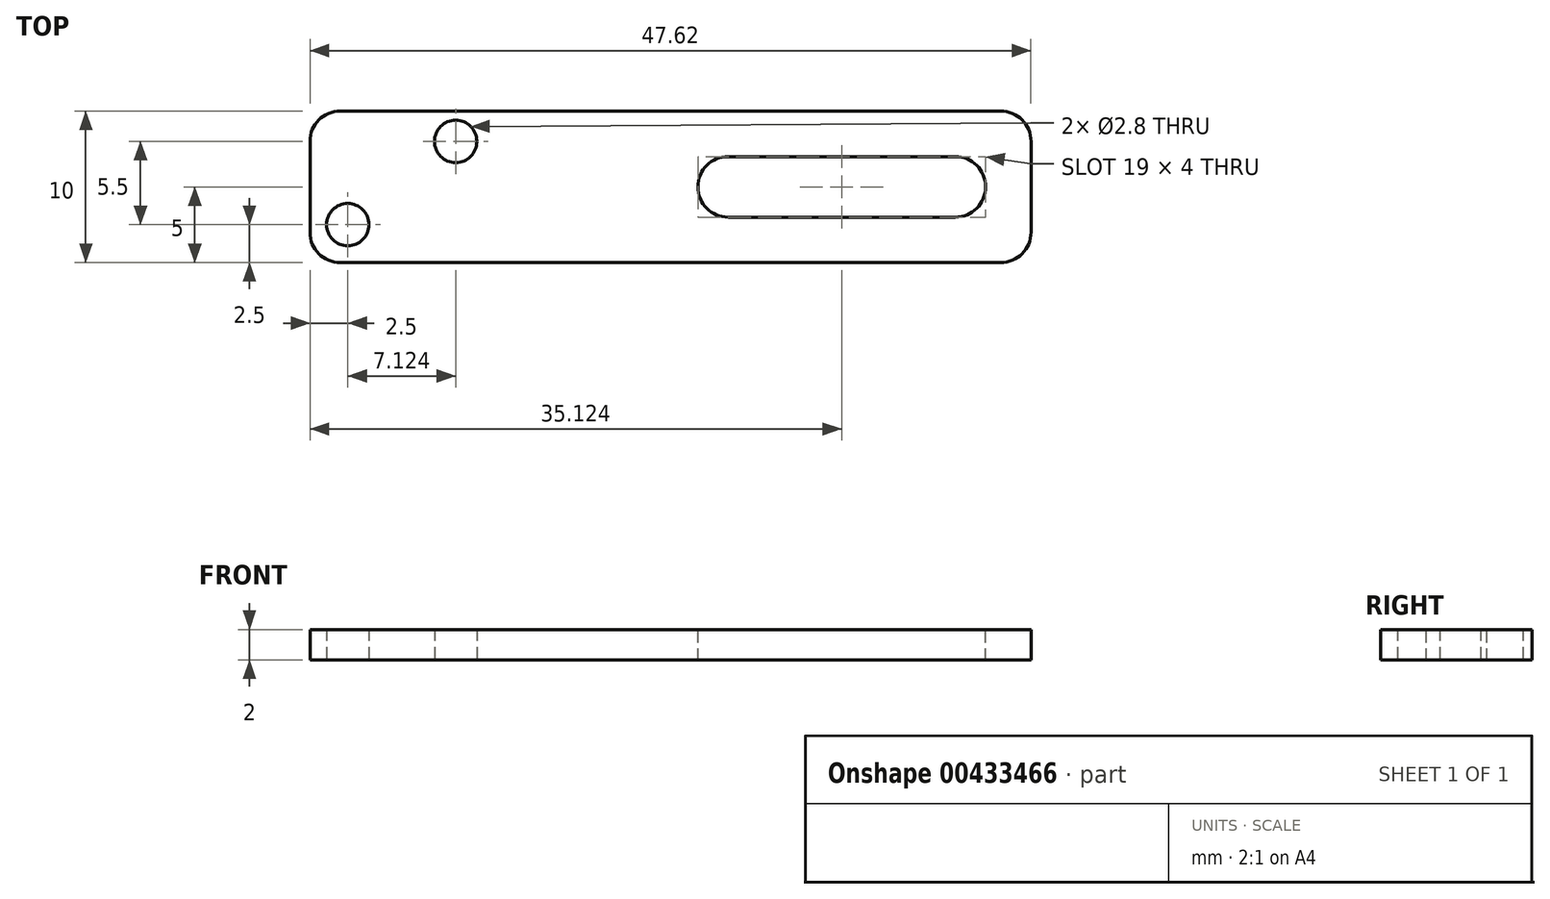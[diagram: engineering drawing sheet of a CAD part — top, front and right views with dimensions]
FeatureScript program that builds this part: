
annotation { "Feature Type Name" : "Feature", "Feature Type Description" : "" }
export const myFeature = defineFeature(function(context is Context, id is Id, definition is map)
    precondition{}
    {
        {
            var Q0;
            Q0=qCreatedBy(makeId("Top.planeOp"),FACE);
            var sketch = newSketch(context, id + "F0", { "sketchPlane" : qUnion([Q0])});
            skLineSegment(sketch, "E0", {"start": v(47.62, 10) * mm, "end": v(13.02, 10) * mm});
            skLineSegment(sketch, "E1", {"start": v(13.02, 10) * mm, "end": v(13.02, 10) * mm});
            skLineSegment(sketch, "E2", {"start": v(13.02, 10) * mm, "end": v(0, 10) * mm});
            skLineSegment(sketch, "E3", {"start": v(0, 10) * mm, "end": v(0, 0) * mm});
            skLineSegment(sketch, "E4", {"start": v(0, 0) * mm, "end": v(47.62, 0) * mm});
            skLineSegment(sketch, "E5", {"start": v(47.62, 0) * mm, "end": v(47.62, 10) * mm});
            skCircle(sketch, "E6", {"center": v(9.62, 8) * mm, "radius": 1.4 * mm});
            skCircle(sketch, "E7", {"center": v(2.5, 2.5) * mm, "radius": 1.4 * mm});
            skSolve(sketch);
        }
        {
            var Q0;
            Q0 = qSketchRegion(id + "F0", true);
            extrude(context, id + "F1", {"entities" : qUnion([Q0]), "depth" : 2 * mm});
        }
        {
            var Q0;
            Q0=makeQuery(id+"F1.opExtrude","SWEPT_EDGE",EDGE,{"disambiguationData":[OSD([sQuery(id+"F0.wireOp",EDGE,"E3"),sQuery(id+"F0.wireOp",EDGE,"E4")])]});
            var Q1;
            Q1=makeQuery(id+"F1.opExtrude","SWEPT_EDGE",EDGE,{"disambiguationData":[OSD([sQuery(id+"F0.wireOp",EDGE,"E2"),sQuery(id+"F0.wireOp",EDGE,"E3")])]});
            var Q2;
            Q2=makeQuery(id+"F1.opExtrude","SWEPT_EDGE",EDGE,{"disambiguationData":[OSD([sQuery(id+"F0.wireOp",EDGE,"E4"),sQuery(id+"F0.wireOp",EDGE,"E5")])]});
            var Q3;
            Q3=makeQuery(id+"F1.opExtrude","SWEPT_EDGE",EDGE,{"disambiguationData":[OSD([sQuery(id+"F0.wireOp",EDGE,"E0"),sQuery(id+"F0.wireOp",EDGE,"E5")])]});
            fillet(context, id + "F2", {"entities" : qUnion([Q0, Q1, Q2, Q3]), "radius" : 2 * mm, "tangentPropagation" : true, "allowEdgeOverflow" : false});
        }
        {
            var Q0;
            Q0=makeQuery(id+"F1.opExtrude","CAP_FACE",FACE,{"disambiguationData":[OSD([sQuery(id+"F0.wireOp",EDGE,"E0"),sQuery(id+"F0.wireOp",EDGE,"E2"),sQuery(id+"F0.wireOp",EDGE,"E3"),sQuery(id+"F0.wireOp",EDGE,"E4"),sQuery(id+"F0.wireOp",EDGE,"E5"),sQuery(id+"F0.wireOp",EDGE,"E6"),sQuery(id+"F0.wireOp",EDGE,"E7")])],"isStart":false});
            var sketch = newSketch(context, id + "F3", { "sketchPlane" : qUnion([Q0])});
            skLineSegment(sketch, "E8", {"start": v(42.62, 5) * mm, "end": v(27.62, 5) * mm, "construction": true});
            skPoint(sketch, "E8.startSnap0", {"position": v(47.62, 5) * mm});
            skArc(sketch, "E9.0.startCap", {"start": v(42.62, 7) * mm, "mid": v(44.62, 5) * mm, "end": v(42.62, 3) * mm});
            skArc(sketch, "E9.0.endCap", {"start": v(27.62, 3) * mm, "mid": v(25.62, 5) * mm, "end": v(27.62, 7) * mm});
            skLineSegment(sketch, "E9.0.left", {"start": v(42.62, 3) * mm, "end": v(27.62, 3) * mm});
            skLineSegment(sketch, "E9.0.right", {"start": v(42.62, 7) * mm, "end": v(27.62, 7) * mm});
            skSolve(sketch);
        }
        {
            var Q0;
            Q0 = qSketchRegion(id + "F3", true);
            extrude(context, id + "F4", {"entities" : qUnion([Q0]), "operationType" : NewBodyOperationType.REMOVE, "endBound" : BoundingType.THROUGH_ALL, "oppositeDirection" : true, "depth" : 25 * mm});
        }
    });
